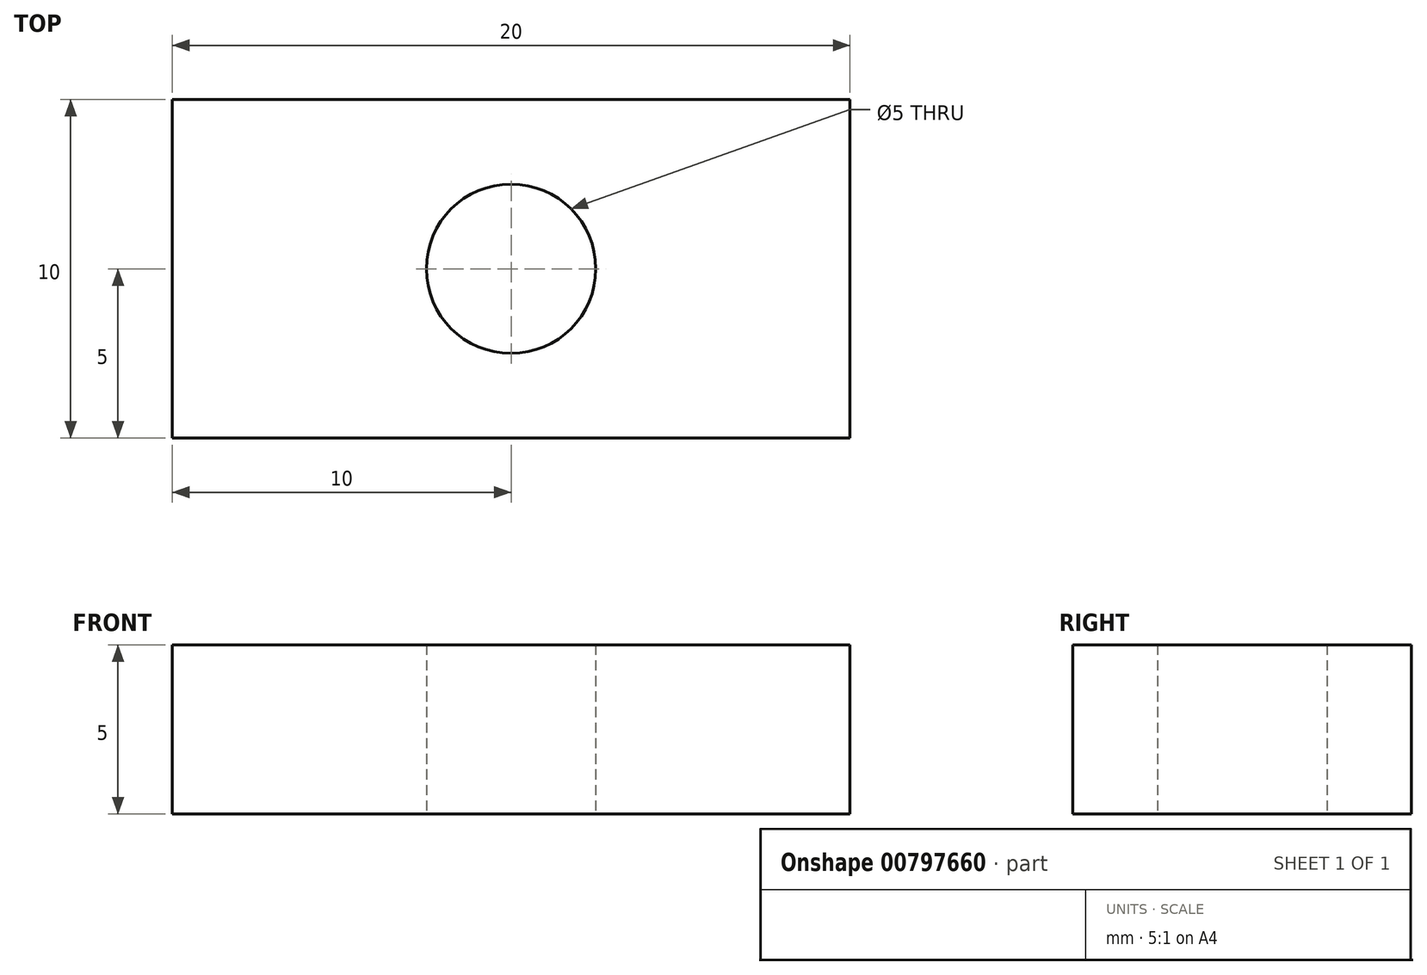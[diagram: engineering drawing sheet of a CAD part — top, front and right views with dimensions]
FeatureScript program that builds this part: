
annotation { "Feature Type Name" : "Feature", "Feature Type Description" : "" }
export const myFeature = defineFeature(function(context is Context, id is Id, definition is map)
    precondition{}
    {
        {
            var Q0;
            Q0=qCreatedBy(makeId("Top.planeOp"),FACE);
            var sketch = newSketch(context, id + "F0", { "sketchPlane" : qUnion([Q0])});
            skLineSegment(sketch, "E0.bottom", {"start": v(0, 0) * mm, "end": v(20, 0) * mm});
            skLineSegment(sketch, "E0.top", {"start": v(0, 10) * mm, "end": v(20, 10) * mm});
            skLineSegment(sketch, "E0.left", {"start": v(0, 0) * mm, "end": v(0, 10) * mm});
            skLineSegment(sketch, "E0.right", {"start": v(20, 0) * mm, "end": v(20, 10) * mm});
            skLineSegment(sketch, "E1", {"start": v(0, 5) * mm, "end": v(10, 5) * mm, "construction": true});
            skCircle(sketch, "E2", {"center": v(10, 5) * mm, "radius": 2.5 * mm});
            skSolve(sketch);
        }
        {
            var Q0;
            Q0=makeQuery(id+"F0.imprint","IMPRINT",FACE,{"disambiguationData":[TD([[makeQuery(id+"F0.imprint","IMPRINT",EDGE,{"derivedFrom":sQuery(id+"F0.wireOp",EDGE,"E0.bottom")}),1.0]])]});
            extrude(context, id + "F1", {"entities" : qUnion([Q0]), "depth" : 5 * mm, "offsetDistance" : 25 * mm});
        }
    });
